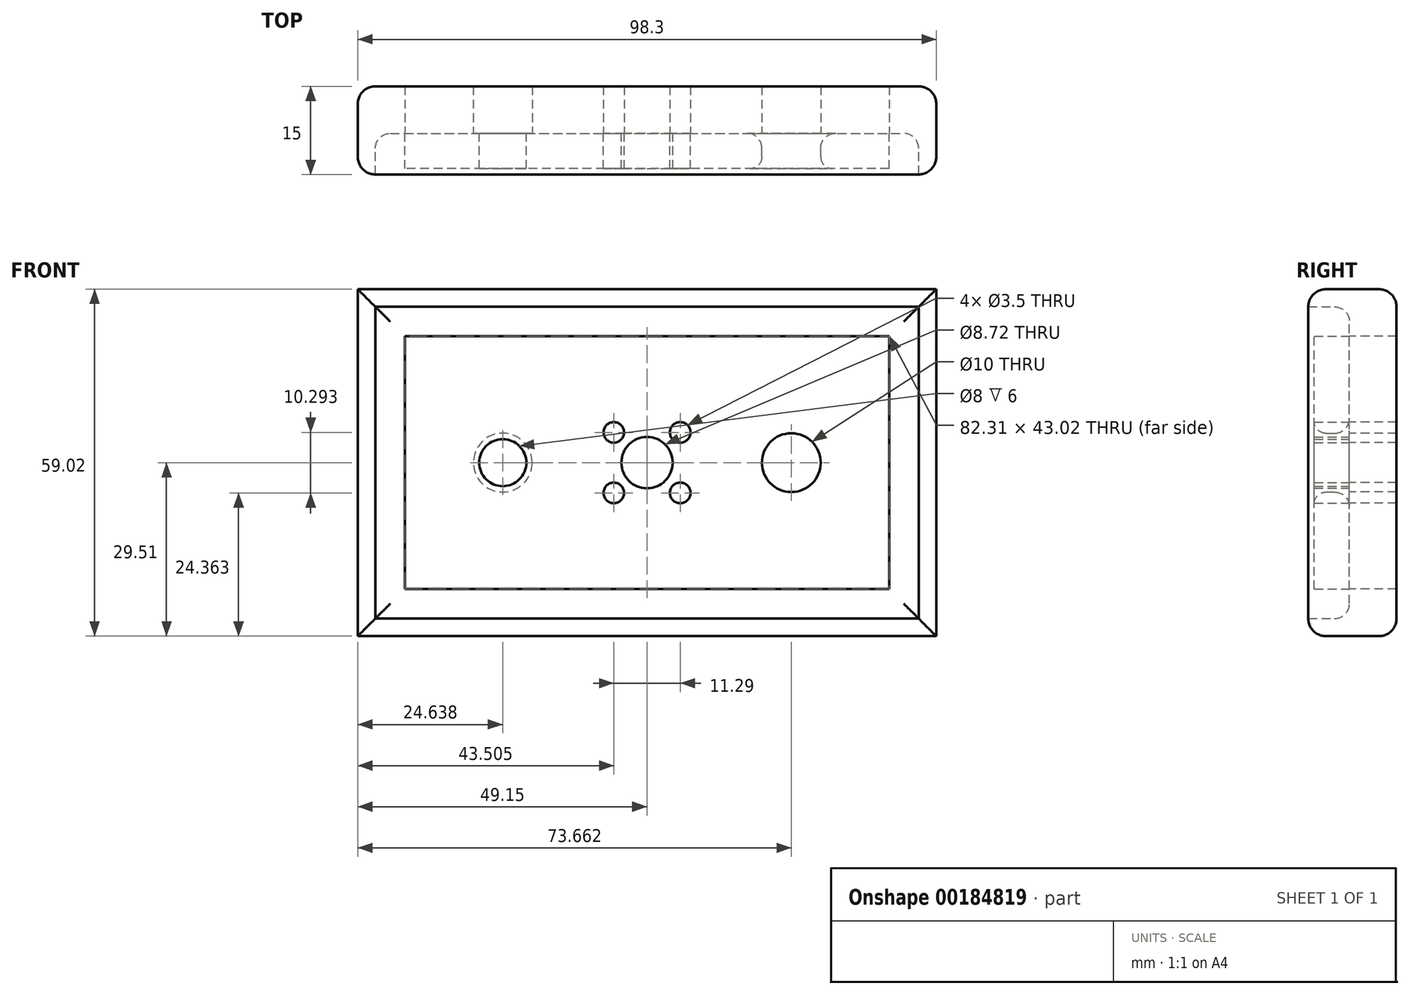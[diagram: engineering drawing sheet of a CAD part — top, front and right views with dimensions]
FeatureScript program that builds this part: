
annotation { "Feature Type Name" : "Feature", "Feature Type Description" : "" }
export const myFeature = defineFeature(function(context is Context, id is Id, definition is map)
    precondition{}
    {
        {
            var Q0;
            Q0=qCreatedBy(makeId("Front.planeOp"),FACE);
            var sketch = newSketch(context, id + "F0", { "sketchPlane" : qUnion([Q0])});
            skLineSegment(sketch, "E0.bottom", {"start": v(46.15, 26.5) * mm, "end": v(-46.15, 26.5) * mm});
            skLineSegment(sketch, "E0.top", {"start": v(46.15, -26.5) * mm, "end": v(-46.15, -26.5) * mm});
            skLineSegment(sketch, "E0.left", {"start": v(46.15, 26.5) * mm, "end": v(46.15, -26.5) * mm});
            skLineSegment(sketch, "E0.right", {"start": v(-46.15, 26.5) * mm, "end": v(-46.15, -26.5) * mm});
            skPoint(sketch, "E0.middle", {"position": v(0, 0) * mm});
            skLineSegment(sketch, "E1.0", {"start": v(49.15, 29.5) * mm, "end": v(-49.15, 29.5) * mm});
            skLineSegment(sketch, "E1.1", {"start": v(49.15, 29.5) * mm, "end": v(49.15, -29.5) * mm});
            skLineSegment(sketch, "E1.2", {"start": v(49.15, -29.5) * mm, "end": v(-49.15, -29.5) * mm});
            skLineSegment(sketch, "E1.3", {"start": v(-49.15, 29.5) * mm, "end": v(-49.15, -29.5) * mm});
            skSolve(sketch);
        }
        {
            var Q0;
            Q0=makeQuery(id+"F0.imprint","IMPRINT",FACE,{"disambiguationData":[TD([[makeQuery(id+"F0.imprint","IMPRINT",EDGE,{"derivedFrom":sQuery(id+"F0.wireOp",EDGE,"E0.bottom")}),1.0]])]});
            var Q1;
            Q1=makeQuery(id+"F0.imprint","IMPRINT",FACE,{"disambiguationData":[TD([[makeQuery(id+"F0.imprint","IMPRINT",EDGE,{"derivedFrom":sQuery(id+"F0.wireOp",EDGE,"E0.bottom")}),-1.0]])]});
            extrude(context, id + "F1", {"entities" : qUnion([Q0, Q1]), "depth" : 8 * mm});
        }
        {
            var Q0;
            Q0=qSketchRegion(id+"F0",true);
            extrude(context, id + "F2", {"entities" : qUnion([Q0]), "operationType" : NewBodyOperationType.ADD, "depth" : 15 * mm});
        }
        {
            var Q0;
            Q0=makeQuery(id+"F1.opExtrude","CAP_FACE",FACE,{"disambiguationData":[OSD([sQuery(id+"F0.wireOp",EDGE,"E1.0"),sQuery(id+"F0.wireOp",EDGE,"E1.1"),sQuery(id+"F0.wireOp",EDGE,"E1.2"),sQuery(id+"F0.wireOp",EDGE,"E1.3")])],"isStart":false});
            var sketch = newSketch(context, id + "F3", { "sketchPlane" : qUnion([Q0])});
            skCircle(sketch, "E2", {"center": v(0, 0) * mm, "radius": 4.36 * mm});
            skCircle(sketch, "E3", {"center": v(-5.64, 5.15) * mm, "radius": 1.75 * mm});
            skCircle(sketch, "E4.MirrorC", {"center": v(5.64, 5.15) * mm, "radius": 1.75 * mm});
            skCircle(sketch, "E5.MirrorC", {"center": v(-5.64, -5.15) * mm, "radius": 1.75 * mm});
            skCircle(sketch, "E6.MirrorC", {"center": v(5.64, -5.15) * mm, "radius": 1.75 * mm});
            skLineSegment(sketch, "E7.0", {"start": v(41.15, 21.5) * mm, "end": v(-41.15, 21.5) * mm});
            skLineSegment(sketch, "E7.1", {"start": v(41.15, -21.5) * mm, "end": v(41.15, 21.5) * mm});
            skLineSegment(sketch, "E7.2", {"start": v(-41.15, -21.5) * mm, "end": v(41.15, -21.5) * mm});
            skLineSegment(sketch, "E7.3", {"start": v(-41.15, 21.5) * mm, "end": v(-41.15, -21.5) * mm});
            skCircle(sketch, "E8", {"center": v(-24.51, 0) * mm, "radius": 4 * mm});
            skCircle(sketch, "E9.0", {"center": v(-24.51, 0) * mm, "radius": 5 * mm});
            skCircle(sketch, "E10.MirrorC", {"center": v(24.51, 0) * mm, "radius": 5 * mm});
            skCircle(sketch, "E11.MirrorC", {"center": v(24.51, 0) * mm, "radius": 4 * mm});
            skSolve(sketch);
        }
        {
            var Q0;
            Q0=makeQuery(id+"F3.imprint","IMPRINT",FACE,{"disambiguationData":[TD([[makeQuery(id+"F3.imprint","IMPRINT",EDGE,{"derivedFrom":sQuery(id+"F3.wireOp",EDGE,"E2")}),1.0]])]});
            var Q1;
            Q1=makeQuery(id+"F3.imprint","IMPRINT",FACE,{"disambiguationData":[TD([[makeQuery(id+"F3.imprint","IMPRINT",EDGE,{"derivedFrom":sQuery(id+"F3.wireOp",EDGE,"E4.MirrorC")}),-1.0]])]});
            var Q2;
            Q2=makeQuery(id+"F3.imprint","IMPRINT",FACE,{"disambiguationData":[TD([[makeQuery(id+"F3.imprint","IMPRINT",EDGE,{"derivedFrom":sQuery(id+"F3.wireOp",EDGE,"E3")}),1.0]])]});
            var Q3;
            Q3=makeQuery(id+"F3.imprint","IMPRINT",FACE,{"disambiguationData":[TD([[makeQuery(id+"F3.imprint","IMPRINT",EDGE,{"derivedFrom":sQuery(id+"F3.wireOp",EDGE,"E5.MirrorC")}),-1.0]])]});
            var Q4;
            Q4=makeQuery(id+"F3.imprint","IMPRINT",FACE,{"disambiguationData":[TD([[makeQuery(id+"F3.imprint","IMPRINT",EDGE,{"derivedFrom":sQuery(id+"F3.wireOp",EDGE,"E6.MirrorC")}),1.0]])]});
            extrude(context, id + "F4", {"entities" : qUnion([Q0, Q1, Q2, Q3, Q4]), "operationType" : NewBodyOperationType.REMOVE, "endBound" : BoundingType.THROUGH_ALL, "oppositeDirection" : true, "depth" : 25 * mm});
        }
        {
            var Q0;
            Q0=makeQuery(id+"F3.imprint","IMPRINT",FACE,{"disambiguationData":[TD([[makeQuery(id+"F3.imprint","IMPRINT",EDGE,{"derivedFrom":sQuery(id+"F3.wireOp",EDGE,"E8")}),-1.0]])]});
            var Q1;
            Q1=makeQuery(id+"F3.imprint","IMPRINT",FACE,{"disambiguationData":[TD([[makeQuery(id+"F3.imprint","IMPRINT",EDGE,{"derivedFrom":sQuery(id+"F3.wireOp",EDGE,"E10.MirrorC")}),-1.0]])]});
            extrude(context, id + "F5", {"entities" : qUnion([Q0, Q1]), "operationType" : NewBodyOperationType.ADD, "depth" : 6 * mm});
        }
        {
            var Q0;
            Q0=makeQuery(id+"F5.opExtrude","CAP_EDGE",EDGE,{"disambiguationData":[OSD([sQuery(id+"F3.wireOp",EDGE,"E9.0")])],"isStart":true});
            var Q1;
            Q1=makeQuery(id+"F5.opExtrude","CAP_EDGE",EDGE,{"disambiguationData":[OSD([sQuery(id+"F3.wireOp",EDGE,"E10.MirrorC")])],"isStart":true});
            var Q2;
            Q2=makeQuery(id+"F2.boolean.opBoolean","INTERSECT",EDGE,{"derivedFrom":[makeQuery(id+"F1.opExtrude","CAP_FACE",FACE,{"disambiguationData":[OSD([sQuery(id+"F0.wireOp",EDGE,"E1.0"),sQuery(id+"F0.wireOp",EDGE,"E1.1"),sQuery(id+"F0.wireOp",EDGE,"E1.2"),sQuery(id+"F0.wireOp",EDGE,"E1.3")])],"isStart":false}),makeQuery(id+"F2.opExtrude","SWEPT_FACE",FACE,{"disambiguationData":[OSD([sQuery(id+"F0.wireOp",EDGE,"E0.top")])]})]});
            var Q3;
            Q3=makeQuery(id+"F2.boolean.opBoolean","INTERSECT",EDGE,{"derivedFrom":[makeQuery(id+"F1.opExtrude","CAP_FACE",FACE,{"disambiguationData":[OSD([sQuery(id+"F0.wireOp",EDGE,"E1.0"),sQuery(id+"F0.wireOp",EDGE,"E1.1"),sQuery(id+"F0.wireOp",EDGE,"E1.2"),sQuery(id+"F0.wireOp",EDGE,"E1.3")])],"isStart":false}),makeQuery(id+"F2.opExtrude","SWEPT_FACE",FACE,{"disambiguationData":[OSD([sQuery(id+"F0.wireOp",EDGE,"E0.left")])]})]});
            var Q4;
            Q4=makeQuery(id+"F2.boolean.opBoolean","INTERSECT",EDGE,{"derivedFrom":[makeQuery(id+"F1.opExtrude","CAP_FACE",FACE,{"disambiguationData":[OSD([sQuery(id+"F0.wireOp",EDGE,"E1.0"),sQuery(id+"F0.wireOp",EDGE,"E1.1"),sQuery(id+"F0.wireOp",EDGE,"E1.2"),sQuery(id+"F0.wireOp",EDGE,"E1.3")])],"isStart":false}),makeQuery(id+"F2.opExtrude","SWEPT_FACE",FACE,{"disambiguationData":[OSD([sQuery(id+"F0.wireOp",EDGE,"E0.right")])]})]});
            var Q5;
            Q5=makeQuery(id+"F2.boolean.opBoolean","INTERSECT",EDGE,{"derivedFrom":[makeQuery(id+"F1.opExtrude","CAP_FACE",FACE,{"disambiguationData":[OSD([sQuery(id+"F0.wireOp",EDGE,"E1.0"),sQuery(id+"F0.wireOp",EDGE,"E1.1"),sQuery(id+"F0.wireOp",EDGE,"E1.2"),sQuery(id+"F0.wireOp",EDGE,"E1.3")])],"isStart":false}),makeQuery(id+"F2.opExtrude","SWEPT_FACE",FACE,{"disambiguationData":[OSD([sQuery(id+"F0.wireOp",EDGE,"E0.bottom")])]})]});
            fillet(context, id + "F6", {"entities" : qUnion([Q0, Q1, Q2, Q3, Q4, Q5]), "radius" : 2.54 * mm, "tangentPropagation" : true, "allowEdgeOverflow" : false});
        }
        {
            var Q0;
            Q0=makeQuery(id+"F3.imprint","IMPRINT",FACE,{"disambiguationData":[TD([[makeQuery(id+"F3.imprint","IMPRINT",EDGE,{"derivedFrom":sQuery(id+"F3.wireOp",EDGE,"E2")}),-1.0]])]});
            var sketch = newSketch(context, id + "F7", { "sketchPlane" : qUnion([Q0])});
            skCircle(sketch, "E12.cCircle", {"center": v(-5.64, 5.1) * mm, "radius": 2.73 * mm, "construction": true});
            skLineSegment(sketch, "E12.0", {"start": v(-4.22, 7.43) * mm, "end": v(-2.9, 5.04) * mm});
            skLineSegment(sketch, "E12.1", {"start": v(-2.9, 5.04) * mm, "end": v(-4.32, 2.7) * mm});
            skLineSegment(sketch, "E12.2", {"start": v(-4.32, 2.7) * mm, "end": v(-7.05, 2.76) * mm});
            skLineSegment(sketch, "E12.3", {"start": v(-7.05, 2.76) * mm, "end": v(-8.37, 5.15) * mm});
            skLineSegment(sketch, "E12.4", {"start": v(-8.37, 5.15) * mm, "end": v(-6.96, 7.49) * mm});
            skLineSegment(sketch, "E12.5", {"start": v(-6.96, 7.49) * mm, "end": v(-4.22, 7.43) * mm});
            skCircle(sketch, "E13.MirrorC", {"center": v(5.64, 5.1) * mm, "radius": 2.73 * mm, "construction": true});
            skLineSegment(sketch, "E14.MirrorCS", {"start": v(6.96, 7.49) * mm, "end": v(4.22, 7.43) * mm});
            skLineSegment(sketch, "E15.MirrorCS", {"start": v(8.37, 5.15) * mm, "end": v(6.96, 7.49) * mm});
            skLineSegment(sketch, "E16.MirrorCS", {"start": v(7.05, 2.76) * mm, "end": v(8.37, 5.15) * mm});
            skLineSegment(sketch, "E17.MirrorCS", {"start": v(4.32, 2.7) * mm, "end": v(7.05, 2.76) * mm});
            skLineSegment(sketch, "E18.MirrorCS", {"start": v(2.9, 5.04) * mm, "end": v(4.32, 2.7) * mm});
            skLineSegment(sketch, "E19.MirrorCS", {"start": v(4.22, 7.43) * mm, "end": v(2.9, 5.04) * mm});
            skCircle(sketch, "E20.MirrorC", {"center": v(-5.64, -5.1) * mm, "radius": 2.73 * mm, "construction": true});
            skLineSegment(sketch, "E21.MirrorCS", {"start": v(-4.32, -2.7) * mm, "end": v(-7.05, -2.76) * mm});
            skLineSegment(sketch, "E22.MirrorCS", {"start": v(-6.96, -7.49) * mm, "end": v(-4.22, -7.43) * mm});
            skLineSegment(sketch, "E23.MirrorCS", {"start": v(-8.37, -5.15) * mm, "end": v(-6.96, -7.49) * mm});
            skLineSegment(sketch, "E24.MirrorCS", {"start": v(-2.9, -5.04) * mm, "end": v(-4.32, -2.7) * mm});
            skLineSegment(sketch, "E25.MirrorCS", {"start": v(-7.05, -2.76) * mm, "end": v(-8.37, -5.15) * mm});
            skLineSegment(sketch, "E26.MirrorCS", {"start": v(-4.22, -7.43) * mm, "end": v(-2.9, -5.04) * mm});
            skCircle(sketch, "E27.MirrorC", {"center": v(5.64, -5.1) * mm, "radius": 2.73 * mm, "construction": true});
            skLineSegment(sketch, "E28.MirrorCS", {"start": v(2.9, -5.04) * mm, "end": v(4.32, -2.7) * mm});
            skLineSegment(sketch, "E29.MirrorCS", {"start": v(4.22, -7.43) * mm, "end": v(2.9, -5.04) * mm});
            skLineSegment(sketch, "E30.MirrorCS", {"start": v(6.96, -7.49) * mm, "end": v(4.22, -7.43) * mm});
            skLineSegment(sketch, "E31.MirrorCS", {"start": v(8.37, -5.15) * mm, "end": v(6.96, -7.49) * mm});
            skLineSegment(sketch, "E32.MirrorCS", {"start": v(7.05, -2.76) * mm, "end": v(8.37, -5.15) * mm});
            skLineSegment(sketch, "E33.MirrorCS", {"start": v(4.32, -2.7) * mm, "end": v(7.05, -2.76) * mm});
            skSolve(sketch);
        }
        {
            var Q0;
            Q0=makeQuery(id+"F7.imprint","IMPRINT",FACE,{"disambiguationData":[TD([[makeQuery(id+"F7.imprint","IMPRINT",EDGE,{"derivedFrom":sQuery(id+"F7.wireOp",EDGE,"E12.0")}),-1.0]])]});
            var Q1;
            Q1=makeQuery(id+"F7.imprint","IMPRINT",FACE,{"disambiguationData":[TD([[makeQuery(id+"F7.imprint","IMPRINT",EDGE,{"derivedFrom":sQuery(id+"F7.wireOp",EDGE,"E14.MirrorCS")}),1.0]])]});
            var Q2;
            Q2=makeQuery(id+"F7.imprint","IMPRINT",FACE,{"disambiguationData":[TD([[makeQuery(id+"F7.imprint","IMPRINT",EDGE,{"derivedFrom":sQuery(id+"F7.wireOp",EDGE,"E28.MirrorCS")}),-1.0]])]});
            var Q3;
            Q3=makeQuery(id+"F7.imprint","IMPRINT",FACE,{"disambiguationData":[TD([[makeQuery(id+"F7.imprint","IMPRINT",EDGE,{"derivedFrom":sQuery(id+"F7.wireOp",EDGE,"E21.MirrorCS")}),1.0]])]});
            extrude(context, id + "F8", {"entities" : qUnion([Q0, Q1, Q2, Q3]), "operationType" : NewBodyOperationType.REMOVE, "oppositeDirection" : true, "depth" : 3 * mm});
        }
        {
            var Q0;
            Q0=makeQuery(id+"F1.opExtrude","CAP_EDGE",EDGE,{"disambiguationData":[OSD([sQuery(id+"F0.wireOp",EDGE,"E1.0")])],"isStart":true});
            var Q1;
            Q1=makeQuery(id+"F1.opExtrude","CAP_EDGE",EDGE,{"disambiguationData":[OSD([sQuery(id+"F0.wireOp",EDGE,"E1.1")])],"isStart":true});
            var Q2;
            Q2=makeQuery(id+"F1.opExtrude","CAP_EDGE",EDGE,{"disambiguationData":[OSD([sQuery(id+"F0.wireOp",EDGE,"E1.2")])],"isStart":true});
            var Q3;
            Q3=makeQuery(id+"F1.opExtrude","CAP_EDGE",EDGE,{"disambiguationData":[OSD([sQuery(id+"F0.wireOp",EDGE,"E1.3")])],"isStart":true});
            fillet(context, id + "F9", {"entities" : qUnion([Q0, Q1, Q2, Q3]), "radius" : 3 * mm, "tangentPropagation" : true, "allowEdgeOverflow" : false});
        }
        {
            var Q0;
            Q0=makeQuery(id+"F2.opExtrude","CAP_EDGE",EDGE,{"disambiguationData":[OSD([sQuery(id+"F0.wireOp",EDGE,"E1.2")])],"isStart":false});
            var Q1;
            Q1=makeQuery(id+"F2.opExtrude","CAP_EDGE",EDGE,{"disambiguationData":[OSD([sQuery(id+"F0.wireOp",EDGE,"E1.1")])],"isStart":false});
            var Q2;
            Q2=makeQuery(id+"F2.opExtrude","CAP_EDGE",EDGE,{"disambiguationData":[OSD([sQuery(id+"F0.wireOp",EDGE,"E1.3")])],"isStart":false});
            var Q3;
            Q3=makeQuery(id+"F2.opExtrude","CAP_EDGE",EDGE,{"disambiguationData":[OSD([sQuery(id+"F0.wireOp",EDGE,"E1.0")])],"isStart":false});
            fillet(context, id + "F10", {"entities" : qUnion([Q0, Q1, Q2, Q3]), "radius" : 3 * mm, "tangentPropagation" : true, "allowEdgeOverflow" : false});
        }
        {
            var Q0;
            Q0=makeQuery(id+"F5.opExtrude","CAP_EDGE",EDGE,{"disambiguationData":[OSD([sQuery(id+"F3.wireOp",EDGE,"E10.MirrorC")])],"isStart":false});
            var Q1;
            Q1=makeQuery(id+"F5.opExtrude","CAP_EDGE",EDGE,{"disambiguationData":[OSD([sQuery(id+"F3.wireOp",EDGE,"E9.0")])],"isStart":false});
            fillet(context, id + "F11", {"entities" : qUnion([Q0, Q1]), "radius" : 2 * mm, "tangentPropagation" : true, "allowEdgeOverflow" : false});
        }
    });
